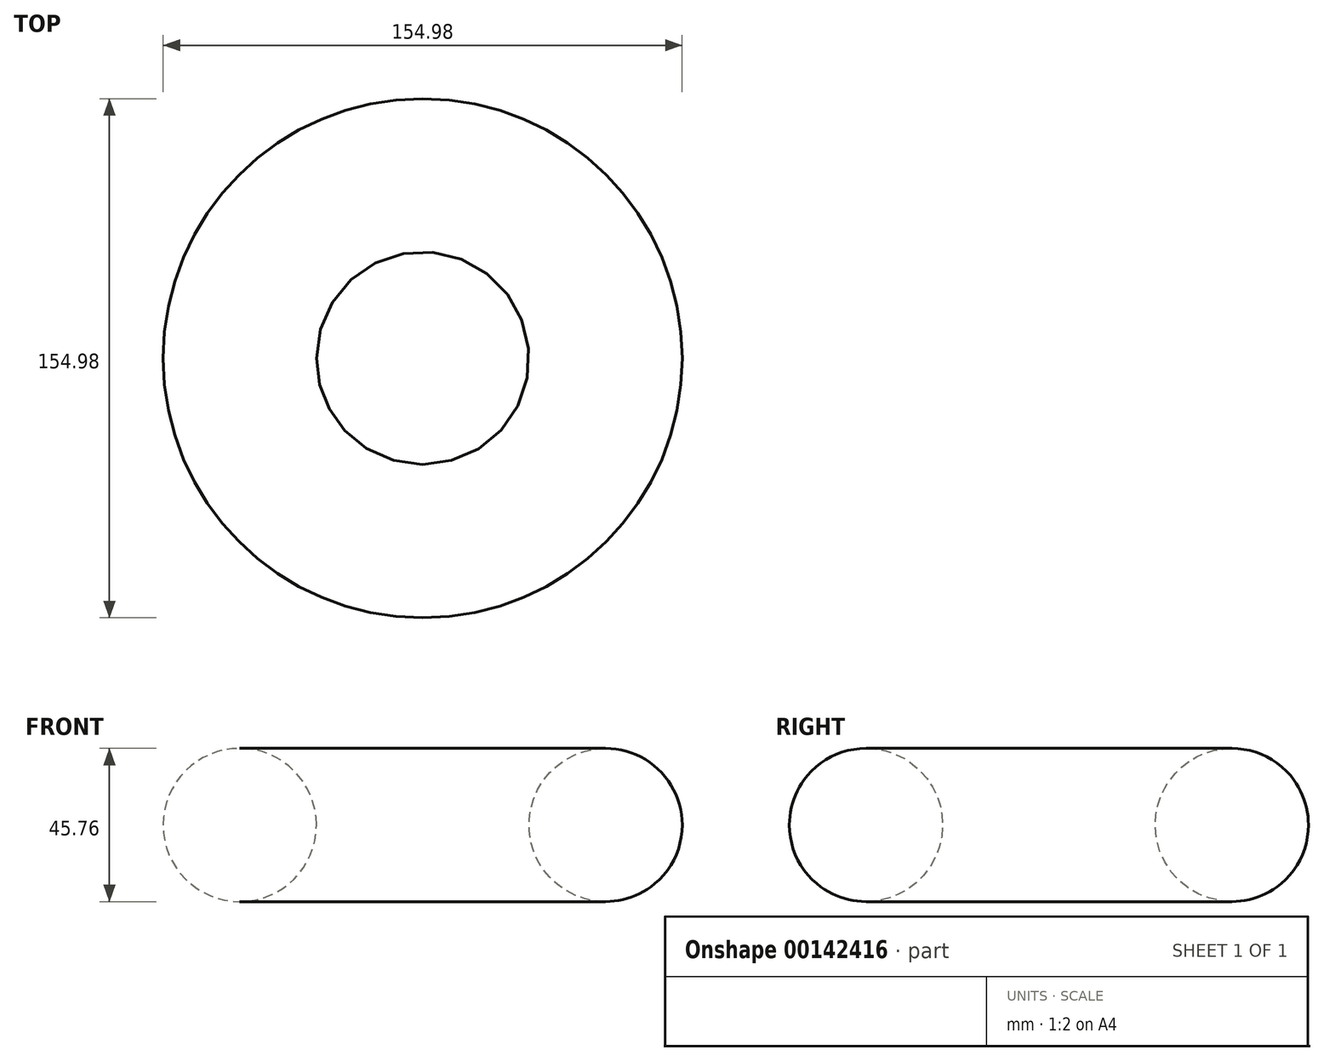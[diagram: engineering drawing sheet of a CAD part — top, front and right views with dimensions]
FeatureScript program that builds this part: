
annotation { "Feature Type Name" : "Feature", "Feature Type Description" : "" }
export const myFeature = defineFeature(function(context is Context, id is Id, definition is map)
    precondition{}
    {
        {
            var Q0;
            Q0=qCreatedBy(makeId("Front.planeOp"),FACE);
            var sketch = newSketch(context, id + "F0", { "sketchPlane" : qUnion([Q0])});
            skCircle(sketch, "E0", {"center": v(54.61, 17.21) * mm, "radius": 22.88 * mm});
            skLineSegment(sketch, "E1", {"start": v(0, 66.37) * mm, "end": v(0, 74.44) * mm});
            skSolve(sketch);
        }
        {
            var Q0;
            Q0 = qSketchRegion(id + "F0", true);
            var Q1;
            Q1=sQuery(id+"F0.wireOp",EDGE,"E1");
            revolve(context, id + "F1", {"entities" : qUnion([Q0]), "axis" : qUnion([Q1]), "revolveType" : RevolveType.FULL});
        }
    });
